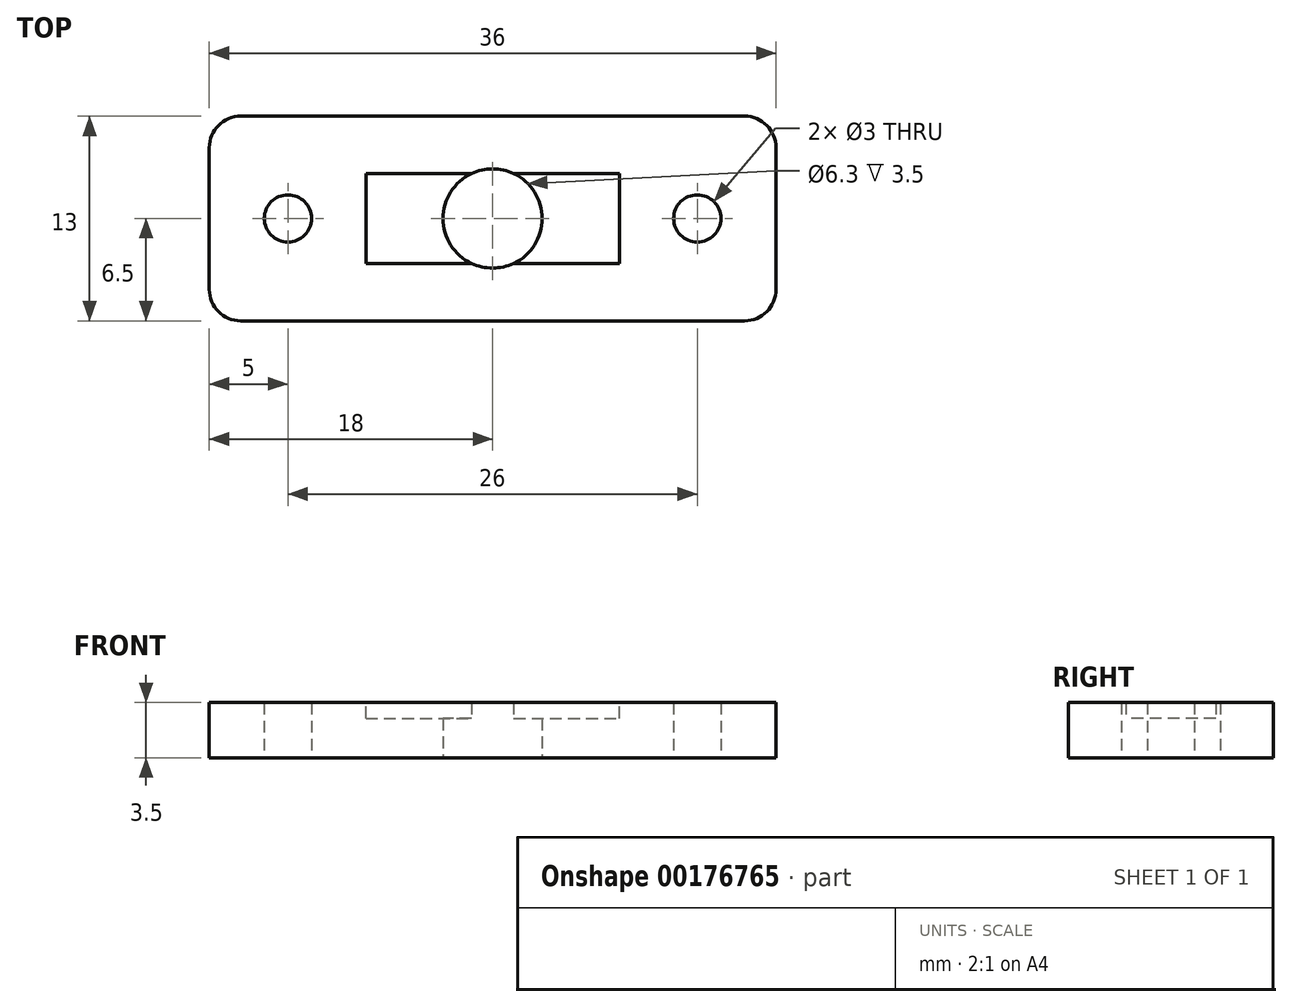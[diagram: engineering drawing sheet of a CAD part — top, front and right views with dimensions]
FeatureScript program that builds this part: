
annotation { "Feature Type Name" : "Feature", "Feature Type Description" : "" }
export const myFeature = defineFeature(function(context is Context, id is Id, definition is map)
    precondition{}
    {
        {
            var Q0;
            Q0=qCreatedBy(makeId("Top.planeOp"),FACE);
            var sketch = newSketch(context, id + "F0", { "sketchPlane" : qUnion([Q0])});
            skLineSegment(sketch, "E0.bottom", {"start": v(-18, 6.5) * mm, "end": v(18, 6.5) * mm});
            skLineSegment(sketch, "E0.top", {"start": v(-18, -6.5) * mm, "end": v(18, -6.5) * mm});
            skLineSegment(sketch, "E0.left", {"start": v(-18, 6.5) * mm, "end": v(-18, -6.5) * mm});
            skLineSegment(sketch, "E0.right", {"start": v(18, 6.5) * mm, "end": v(18, -6.5) * mm});
            skPoint(sketch, "E0.middle", {"position": v(0, 0) * mm});
            skCircle(sketch, "E1", {"center": v(-13, 0) * mm, "radius": 1.5 * mm});
            skCircle(sketch, "E2", {"center": v(13, 0) * mm, "radius": 1.5 * mm});
            skLineSegment(sketch, "E3", {"start": v(-13, 0) * mm, "end": v(0, 0) * mm});
            skLineSegment(sketch, "E4", {"start": v(13, 0) * mm, "end": v(0, 0) * mm});
            skCircle(sketch, "E5", {"center": v(0, 0) * mm, "radius": 3.15 * mm});
            skSolve(sketch);
        }
        {
            var Q0;
            Q0 = qSketchRegion(id + "F0", true);
            extrude(context, id + "F1", {"entities" : qUnion([Q0]), "depth" : 3.5 * mm});
        }
        {
            var Q0;
            Q0=makeQuery(id+"F1.opExtrude","SWEPT_EDGE",EDGE,{"disambiguationData":[OSD([sQuery(id+"F0.wireOp",EDGE,"E0.bottom"),sQuery(id+"F0.wireOp",EDGE,"E0.left")])]});
            var Q1;
            Q1=makeQuery(id+"F1.opExtrude","SWEPT_EDGE",EDGE,{"disambiguationData":[OSD([sQuery(id+"F0.wireOp",EDGE,"E0.top"),sQuery(id+"F0.wireOp",EDGE,"E0.left")])]});
            var Q2;
            Q2=makeQuery(id+"F1.opExtrude","SWEPT_EDGE",EDGE,{"disambiguationData":[OSD([sQuery(id+"F0.wireOp",EDGE,"E0.top"),sQuery(id+"F0.wireOp",EDGE,"E0.right")])]});
            var Q3;
            Q3=makeQuery(id+"F1.opExtrude","SWEPT_EDGE",EDGE,{"disambiguationData":[OSD([sQuery(id+"F0.wireOp",EDGE,"E0.bottom"),sQuery(id+"F0.wireOp",EDGE,"E0.right")])]});
            fillet(context, id + "F2", {"entities" : qUnion([Q0, Q1, Q2, Q3]), "radius" : 2 * mm, "tangentPropagation" : true, "allowEdgeOverflow" : false});
        }
        {
            var Q0;
            Q0=makeQuery(id+"F1.opExtrude","CAP_FACE",FACE,{"disambiguationData":[OSD([sQuery(id+"F0.wireOp",EDGE,"E0.bottom"),sQuery(id+"F0.wireOp",EDGE,"E0.top"),sQuery(id+"F0.wireOp",EDGE,"E0.left"),sQuery(id+"F0.wireOp",EDGE,"E0.right"),sQuery(id+"F0.wireOp",EDGE,"E1"),sQuery(id+"F0.wireOp",EDGE,"E2"),sQuery(id+"F0.wireOp",EDGE,"E5")])],"isStart":false});
            var sketch = newSketch(context, id + "F3", { "sketchPlane" : qUnion([Q0])});
            skLineSegment(sketch, "E6.bottom", {"start": v(-8.05, 2.85) * mm, "end": v(8.05, 2.85) * mm});
            skLineSegment(sketch, "E6.top", {"start": v(-8.05, -2.85) * mm, "end": v(8.05, -2.85) * mm});
            skLineSegment(sketch, "E6.left", {"start": v(-8.05, 2.85) * mm, "end": v(-8.05, -2.85) * mm});
            skLineSegment(sketch, "E6.right", {"start": v(8.05, 2.85) * mm, "end": v(8.05, -2.85) * mm});
            skPoint(sketch, "E6.middle", {"position": v(0, 0) * mm});
            skSolve(sketch);
        }
        {
            var Q0;
            Q0=makeQuery(id+"F3.imprint","IMPRINT",FACE,{"disambiguationData":[TD([[makeQuery(id+"F3.imprint","IMPRINT",EDGE,{"derivedFrom":sQuery(id+"F3.wireOp",EDGE,"E6.bottom")}),-1.0]])]});
            extrude(context, id + "F4", {"entities" : qUnion([Q0]), "operationType" : NewBodyOperationType.REMOVE, "oppositeDirection" : true, "depth" : 1 * mm});
        }
    });
